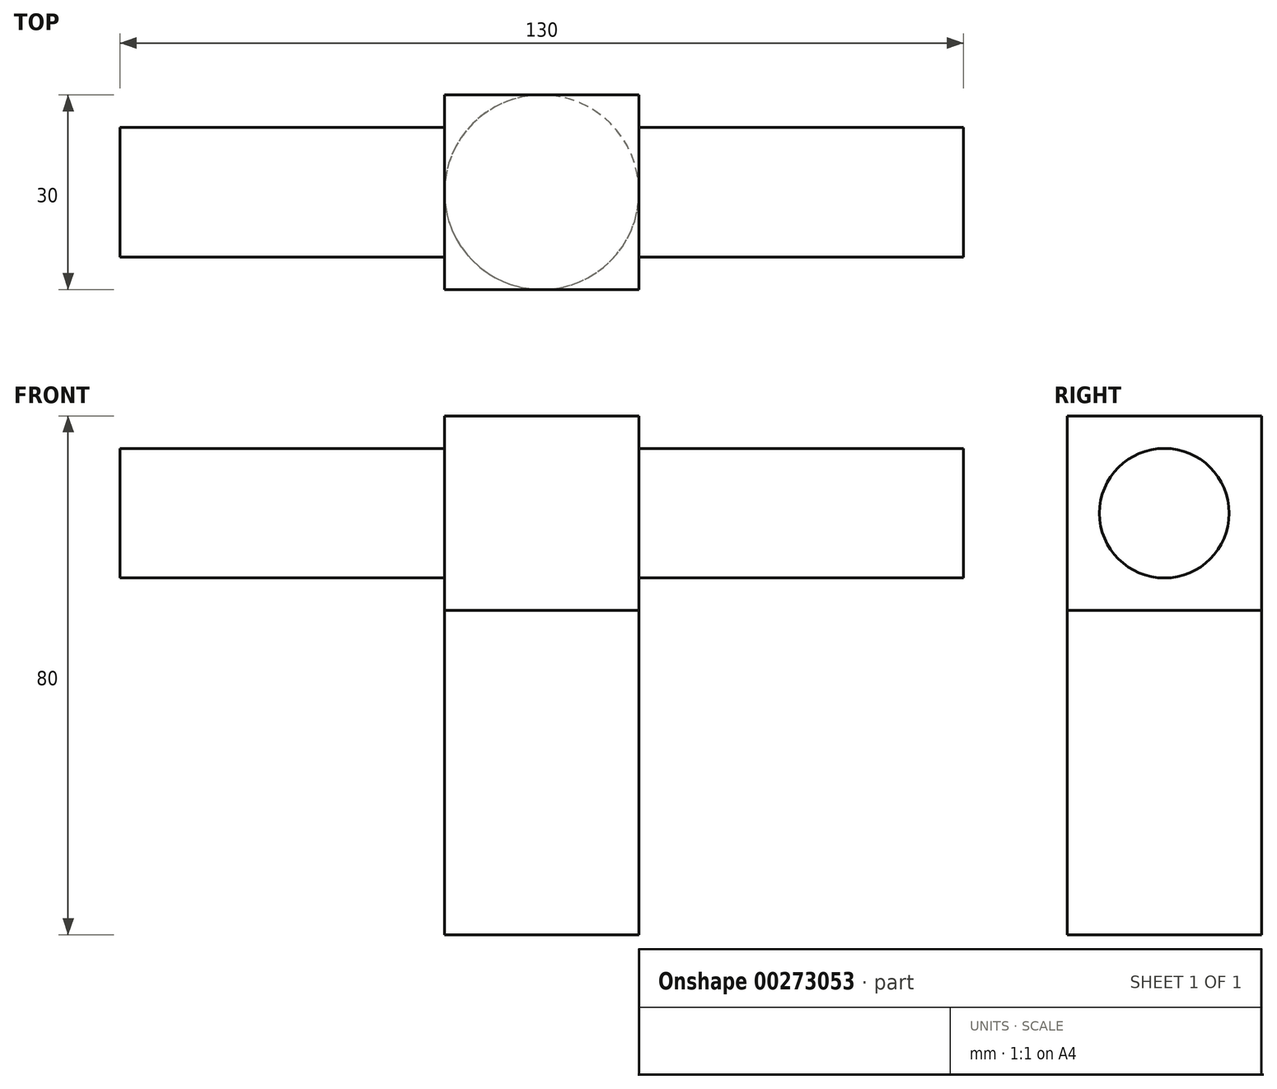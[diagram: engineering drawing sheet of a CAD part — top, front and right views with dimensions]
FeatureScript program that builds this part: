
annotation { "Feature Type Name" : "Feature", "Feature Type Description" : "" }
export const myFeature = defineFeature(function(context is Context, id is Id, definition is map)
    precondition{}
    {
        {
            var Q0;
            Q0=qCreatedBy(makeId("Top.planeOp"),FACE);
            var sketch = newSketch(context, id + "F0", { "sketchPlane" : qUnion([Q0])});
            skLineSegment(sketch, "E0.bottom", {"start": v(15, 15) * mm, "end": v(-15, 15) * mm});
            skLineSegment(sketch, "E0.top", {"start": v(15, -15) * mm, "end": v(-15, -15) * mm});
            skLineSegment(sketch, "E0.left", {"start": v(15, 15) * mm, "end": v(15, -15) * mm});
            skLineSegment(sketch, "E0.right", {"start": v(-15, 15) * mm, "end": v(-15, -15) * mm});
            skPoint(sketch, "E0.middle", {"position": v(0, 0) * mm});
            skSolve(sketch);
        }
        {
            var Q0;
            Q0 = qSketchRegion(id + "F0", true);
            extrude(context, id + "F1", {"entities" : qUnion([Q0]), "depth" : 30 * mm});
        }
        {
            var Q0;
            Q0=makeQuery(id+"F1.opExtrude","CAP_FACE",FACE,{"disambiguationData":[OSD([sQuery(id+"F0.wireOp",EDGE,"E0.bottom"),sQuery(id+"F0.wireOp",EDGE,"E0.top"),sQuery(id+"F0.wireOp",EDGE,"E0.left"),sQuery(id+"F0.wireOp",EDGE,"E0.right")])],"isStart":true});
            var sketch = newSketch(context, id + "F2", { "sketchPlane" : qUnion([Q0])});
            skCircle(sketch, "E1", {"center": v(0, 0) * mm, "radius": 15 * mm});
            skSolve(sketch);
        }
        {
            var Q0;
            Q0 = qSketchRegion(id + "F2", true);
            extrude(context, id + "F3", {"entities" : qUnion([Q0]), "operationType" : NewBodyOperationType.ADD, "depth" : 50 * mm});
        }
        {
            var Q0;
            Q0=makeQuery(id+"F1.opExtrude","SWEPT_FACE",FACE,{"disambiguationData":[OSD([sQuery(id+"F0.wireOp",EDGE,"E0.left")])]});
            var sketch = newSketch(context, id + "F4", { "sketchPlane" : qUnion([Q0])});
            skCircle(sketch, "E2", {"center": v(0, 15) * mm, "radius": 10 * mm});
            skPoint(sketch, "E2.centerSnap0", {"position": v(15, 15) * mm});
            skSolve(sketch);
        }
        {
            var Q0;
            Q0 = qSketchRegion(id + "F4", true);
            extrude(context, id + "F5", {"entities" : qUnion([Q0]), "operationType" : NewBodyOperationType.ADD, "depth" : 50 * mm});
        }
        {
            var Q0;
            Q0=makeQuery(id+"F1.opExtrude","SWEPT_FACE",FACE,{"disambiguationData":[OSD([sQuery(id+"F0.wireOp",EDGE,"E0.right")])]});
            var sketch = newSketch(context, id + "F6", { "sketchPlane" : qUnion([Q0])});
            skCircle(sketch, "E3", {"center": v(0, 15) * mm, "radius": 10 * mm});
            skPoint(sketch, "E3.centerSnap0", {"position": v(15, 15) * mm});
            skSolve(sketch);
        }
        {
            var Q0;
            Q0 = qSketchRegion(id + "F6", true);
            extrude(context, id + "F7", {"entities" : qUnion([Q0]), "operationType" : NewBodyOperationType.ADD, "depth" : 50 * mm});
        }
    });
